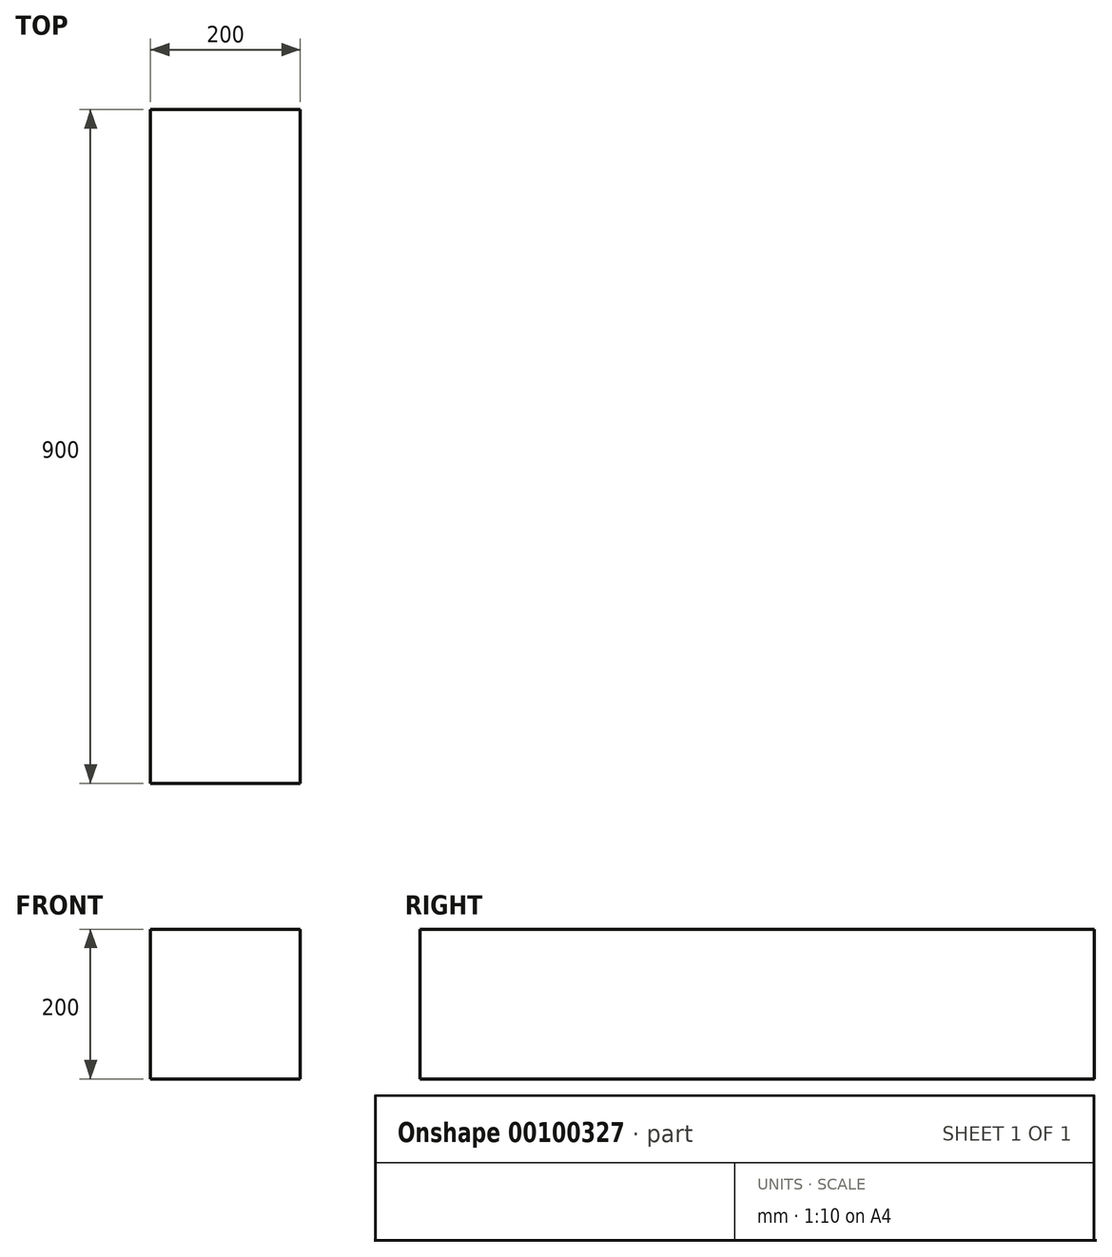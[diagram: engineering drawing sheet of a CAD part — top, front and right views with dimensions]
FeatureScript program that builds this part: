
annotation { "Feature Type Name" : "Feature", "Feature Type Description" : "" }
export const myFeature = defineFeature(function(context is Context, id is Id, definition is map)
    precondition{}
    {
        {
            var Q0;
            Q0=qCreatedBy(makeId("Front.planeOp"),FACE);
            var sketch = newSketch(context, id + "F0", { "sketchPlane" : qUnion([Q0])});
            skLineSegment(sketch, "E0.bottom", {"start": v(-108.99, 99.67) * mm, "end": v(91.01, 99.67) * mm});
            skLineSegment(sketch, "E0.top", {"start": v(-108.99, -100.33) * mm, "end": v(91.01, -100.33) * mm});
            skLineSegment(sketch, "E0.left", {"start": v(-108.99, 99.67) * mm, "end": v(-108.99, -100.33) * mm});
            skLineSegment(sketch, "E0.right", {"start": v(91.01, 99.67) * mm, "end": v(91.01, -100.33) * mm});
            skSolve(sketch);
        }
        {
            var Q0;
            Q0 = qSketchRegion(id + "F0", true);
            extrude(context, id + "F1", {"entities" : qUnion([Q0]), "depth" : 900 * mm});
        }
    });
